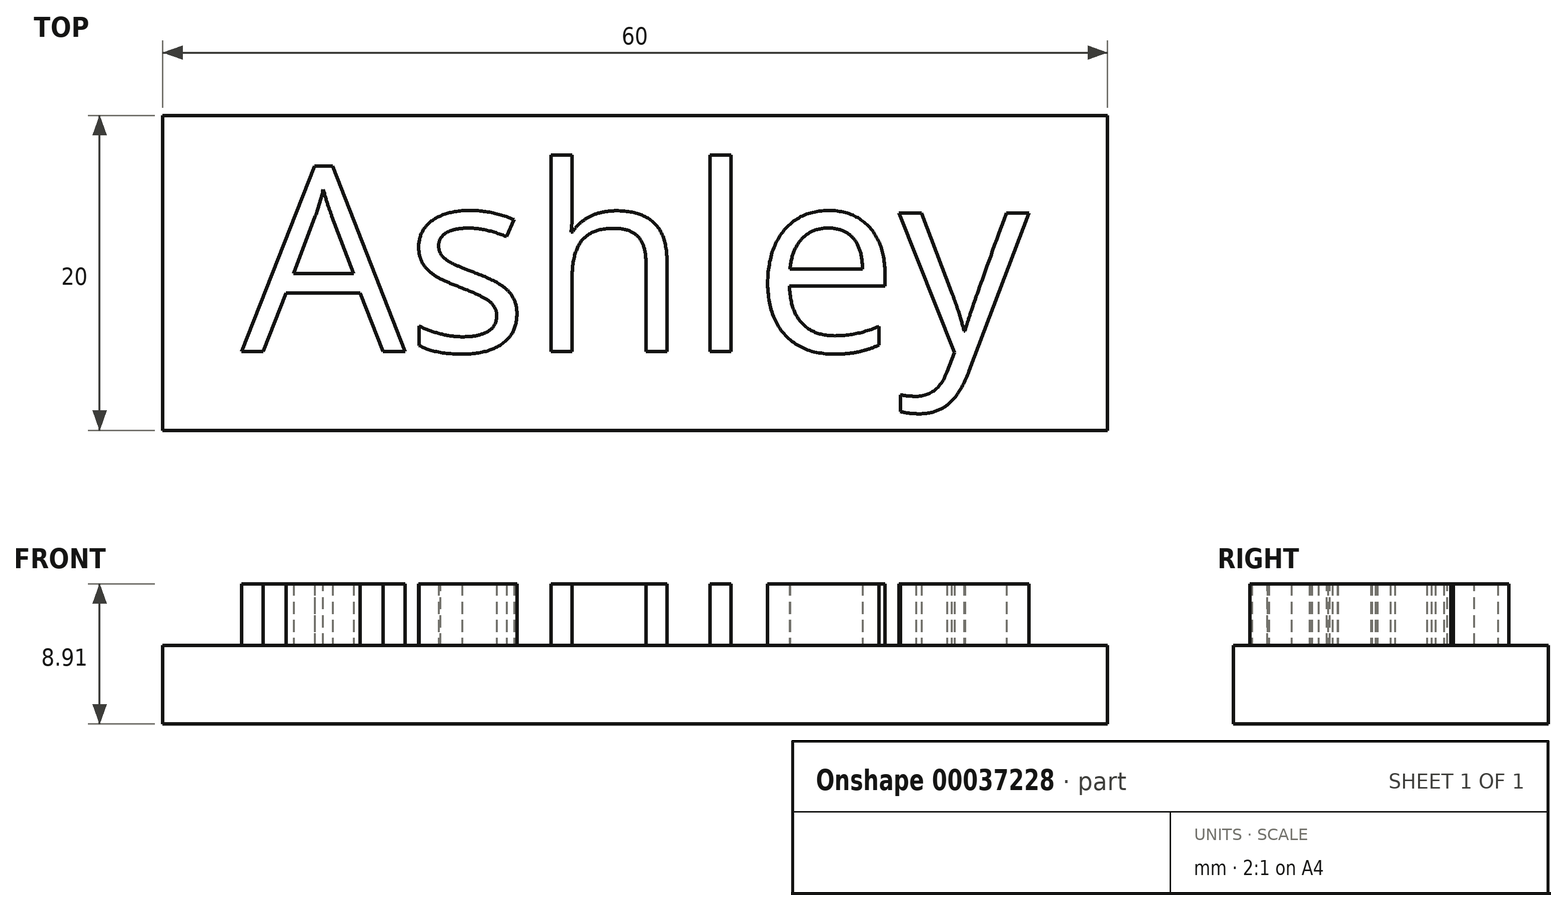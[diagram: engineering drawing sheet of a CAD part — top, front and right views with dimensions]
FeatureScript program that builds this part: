
annotation { "Feature Type Name" : "Feature", "Feature Type Description" : "" }
export const myFeature = defineFeature(function(context is Context, id is Id, definition is map)
    precondition{}
    {
        {
            var Q0;
            Q0=qCreatedBy(makeId("Top.planeOp"),FACE);
            var sketch = newSketch(context, id + "F0", { "sketchPlane" : qUnion([Q0])});
            skLineSegment(sketch, "E0.rect.bottom", {"start": v(-30, 10) * mm, "end": v(30, 10) * mm});
            skLineSegment(sketch, "E0.rect.top", {"start": v(-30, -10) * mm, "end": v(30, -10) * mm});
            skLineSegment(sketch, "E0.rect.left", {"start": v(-30, 10) * mm, "end": v(-30, -10) * mm});
            skLineSegment(sketch, "E0.rect.right", {"start": v(30, 10) * mm, "end": v(30, -10) * mm});
            skPoint(sketch, "E0.rect.middle", {"position": v(0, 0) * mm});
            skSolve(sketch);
        }
        {
            var Q0;
            Q0 = qSketchRegion(id + "F0", true);
            extrude(context, id + "F1", {"entities" : qUnion([Q0]), "depth" : 5 * mm});
        }
        {
            var Q0;
            Q0=qCreatedBy(makeId("Top.planeOp"),FACE);
            var sketch = newSketch(context, id + "F2", { "sketchPlane" : qUnion([Q0])});
            skText(sketch, "E1", { "text": "Ashley", "fontName": "OpenSans-Regular.ttf"});
            const initialGuessF2  = {"E1": [-0.025, -0.005, 1, 0, 0.01184]};
            skSetInitialGuess(sketch, initialGuessF2);
            skSolve(sketch);
        }
        {
            var Q0;
            Q0 = qSketchRegion(id + "F2", true);
            extrude(context, id + "F3", {"entities" : qUnion([Q0]), "operationType" : NewBodyOperationType.ADD, "depth" : 8.9 * mm});
        }
    });
